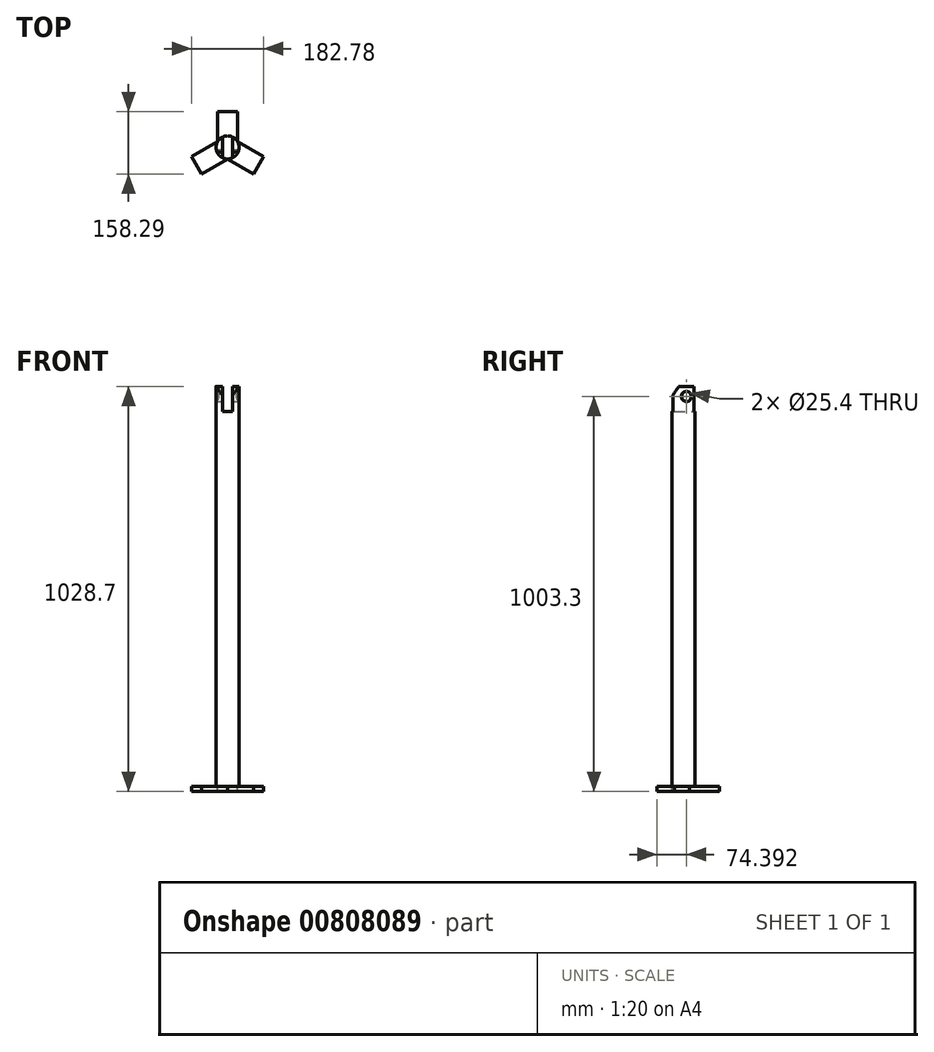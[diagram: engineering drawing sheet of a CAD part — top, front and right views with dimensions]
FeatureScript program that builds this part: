
annotation { "Feature Type Name" : "Feature", "Feature Type Description" : "" }
export const myFeature = defineFeature(function(context is Context, id is Id, definition is map)
    precondition{}
    {
        {
            var Q0;
            Q0=qCreatedBy(makeId("Top.planeOp"),FACE);
            var sketch = newSketch(context, id + "F0", { "sketchPlane" : qUnion([Q0])});
            skPoint(sketch, "E0.middle", {"position": v(0, 0) * mm});
            skLineSegment(sketch, "E1.0", {"start": v(-25.4, 29.33) * mm, "end": v(25.4, 29.33) * mm, "construction": true});
            skLineSegment(sketch, "E1.1", {"start": v(25.4, 29.33) * mm, "end": v(0, -14.66) * mm, "construction": true});
            skLineSegment(sketch, "E1.2", {"start": v(0, -14.66) * mm, "end": v(-25.4, 29.33) * mm, "construction": true});
            skPoint(sketch, "E1.0.midPoint", {"position": v(0, 29.33) * mm});
            skLineSegment(sketch, "E2", {"start": v(-25.4, 29.33) * mm, "end": v(-91.4, -8.77) * mm});
            skLineSegment(sketch, "E3", {"start": v(-91.4, -8.77) * mm, "end": v(-66, -52.76) * mm});
            skLineSegment(sketch, "E4", {"start": v(-66, -52.76) * mm, "end": v(0, -14.66) * mm});
            skLineSegment(sketch, "E5.top", {"start": v(-25.4, 105.53) * mm, "end": v(25.4, 105.53) * mm});
            skLineSegment(sketch, "E5.left", {"start": v(-25.4, 29.33) * mm, "end": v(-25.4, 105.53) * mm});
            skLineSegment(sketch, "E6", {"start": v(0, -14.66) * mm, "end": v(66, -52.76) * mm});
            skLineSegment(sketch, "E7", {"start": v(66, -52.76) * mm, "end": v(91.4, -8.77) * mm});
            skLineSegment(sketch, "E8", {"start": v(91.4, -8.77) * mm, "end": v(25.4, 29.33) * mm});
            skLineSegment(sketch, "E9", {"start": v(25.4, 29.33) * mm, "end": v(25.4, 105.53) * mm});
            skSolve(sketch);
        }
        {
            var Q0;
            Q0=qSketchRegion(id+"F0",true);
            extrude(context, id + "F1", {"entities" : qUnion([Q0]), "oppositeDirection" : true, "depth" : 12.7 * mm, "offsetDistance" : 25.4 * mm});
        }
        {
            var Q0;
            Q0=makeQuery(id+"F1.opExtrude","CAP_FACE",FACE,{"disambiguationData":[OSD([sQuery(id+"F0.wireOp",EDGE,"E2"),sQuery(id+"F0.wireOp",EDGE,"E3"),sQuery(id+"F0.wireOp",EDGE,"E4"),sQuery(id+"F0.wireOp",EDGE,"E5.top"),sQuery(id+"F0.wireOp",EDGE,"E5.left"),sQuery(id+"F0.wireOp",EDGE,"E5.right"),sQuery(id+"F0.wireOp",EDGE,"E6"),sQuery(id+"F0.wireOp",EDGE,"E7"),sQuery(id+"F0.wireOp",EDGE,"E8")])],"isStart":true});
            var sketch = newSketch(context, id + "F2", { "sketchPlane" : qUnion([Q0])});
            skCircle(sketch, "E10", {"center": v(0, 14.66) * mm, "radius": 29.33 * mm});
            skPoint(sketch, "E10.first.point", {"position": v(-25.4, 29.33) * mm});
            skPoint(sketch, "E10.second.point", {"position": v(0, -14.66) * mm});
            skPoint(sketch, "E10.third.point", {"position": v(25.4, 29.33) * mm});
            skSolve(sketch);
        }
        {
            var Q0;
            Q0 = qSketchRegion(id + "F2", true);
            extrude(context, id + "F3", {"entities" : qUnion([Q0]), "operationType" : NewBodyOperationType.ADD, "depth" : 1016 * mm, "offsetDistance" : 25.4 * mm});
        }
        {
            var Q0;
            Q0=makeQuery(id+"F3.opExtrude","CAP_FACE",FACE,{"disambiguationData":[OSD([sQuery(id+"F2.wireOp",EDGE,"E10")])],"isStart":false});
            var sketch = newSketch(context, id + "F4", { "sketchPlane" : qUnion([Q0])});
            skLineSegment(sketch, "E11.bottom", {"start": v(12.7, -17.09) * mm, "end": v(-12.7, -17.09) * mm});
            skLineSegment(sketch, "E11.top", {"start": v(12.7, 46.41) * mm, "end": v(-12.7, 46.41) * mm});
            skLineSegment(sketch, "E11.left", {"start": v(12.7, -17.09) * mm, "end": v(12.7, 46.41) * mm});
            skLineSegment(sketch, "E11.right", {"start": v(-12.7, -17.09) * mm, "end": v(-12.7, 46.41) * mm});
            skPoint(sketch, "E11.middle", {"position": v(0, 14.66) * mm});
            skSolve(sketch);
        }
        {
            var Q0;
            Q0 = qSketchRegion(id + "F4", true);
            extrude(context, id + "F5", {"entities" : qUnion([Q0]), "operationType" : NewBodyOperationType.REMOVE, "oppositeDirection" : true, "depth" : 63.5 * mm, "offsetDistance" : 25.4 * mm});
        }
        {
            var Q0;
            Q0=makeQuery(id+"F5.boolean.opBoolean","COPY",FACE,{"derivedFrom":makeQuery(id+"F5.opExtrude","SWEPT_FACE",FACE,{"disambiguationData":[OSD([sQuery(id+"F4.wireOp",EDGE,"E11.right")])]})});
            var sketch = newSketch(context, id + "F6", { "sketchPlane" : qUnion([Q0])});
            skLineSegment(sketch, "E12.0", {"start": v(-11.77, 1016) * mm, "end": v(-11.77, 994.76) * mm});
            skLineSegment(sketch, "E13.0", {"start": v(-11.77, 1016) * mm, "end": v(2.16, 1016) * mm});
            skLineSegment(sketch, "E14", {"start": v(-11.77, 994.76) * mm, "end": v(2.16, 1016) * mm});
            skPoint(sketch, "E15.orphan", {"position": v(41.1, 1016) * mm});
            skPoint(sketch, "E16.orphan", {"position": v(-11.77, 952.5) * mm});
            skSolve(sketch);
        }
        {
            var Q0;
            Q0 = qSketchRegion(id + "F6", true);
            extrude(context, id + "F7", {"entities" : qUnion([Q0]), "operationType" : NewBodyOperationType.REMOVE, "oppositeDirection" : true, "depth" : 25.4 * mm, "offsetDistance" : 25.4 * mm, "hasSecondDirection" : true, "secondDirectionOppositeDirection" : false, "secondDirectionDepth" : 127 * mm});
        }
        {
            var Q0;
            Q0=makeQuery(id+"F5.boolean.opBoolean","COPY",FACE,{"derivedFrom":makeQuery(id+"F5.opExtrude","SWEPT_FACE",FACE,{"disambiguationData":[OSD([sQuery(id+"F4.wireOp",EDGE,"E11.right")])]})});
            var sketch = newSketch(context, id + "F8", { "sketchPlane" : qUnion([Q0])});
            skCircle(sketch, "E17", {"center": v(21.63, 990.6) * mm, "radius": 12.7 * mm});
            skPoint(sketch, "E17.centerSnap0", {"position": v(21.63, 1016) * mm});
            skSolve(sketch);
        }
        {
            var Q0;
            Q0 = qSketchRegion(id + "F8", true);
            extrude(context, id + "F9", {"entities" : qUnion([Q0]), "operationType" : NewBodyOperationType.REMOVE, "oppositeDirection" : true, "depth" : 25.4 * mm, "offsetDistance" : 25.4 * mm, "hasSecondDirection" : true, "secondDirectionOppositeDirection" : false, "secondDirectionDepth" : 127 * mm});
        }
    });
